# Revit family: Trim_Kit-American_Standard-Delancey-TU05250X_Series
name_source: partatom
category: Plumbing Fixtures
revit_build: Autodesk Revit 2014 (Build: 20130308_1515(x64)
units: mm (PartAtom-declared; Revit-internal decimal feet)

## types (20) — shared parameters
Assembly Code = D2020300
CW Connection = Yes
CWFU = 3
Cold Water Connection Diameter = 1/2"
Cold Water Connection Radius = 1/4"
Default Elevation = 44"
HW Connection = Yes
HWFU = 3
Height = 74"
Hot Water Connection Diameter = 1"
Hot Water Connection Radius = 1/4"
Installation Type = Wall Mounted
Length = 9 1/2"
Manufacturer = American Standard
Price = Prices may vary. Please consult Manufacturer Representative for most up-to-date price list.
URL = https://www.americanstandard-us.com
Valve Trim = Yes
Vent Connection = No
WFU = 4
Warranty Information = Limited Lifetime Function and Finish Warranty
Waste Connection = No
Water Connection Diameter = 1/2"
Water Connection Radius = 1/4"
Width = 7 13/16"

## per-type parameters (varying)
| type | ADA Compliant | Description | Diverter | Finish | Flow Rate | Material | Showerhead | Tub Spout |
| TU052500.002 | Yes | Delancey Trim Kit | No | Metal-American Standard-002-Polished Chrome | 2.5 gpm (9.5 L/min) | Metal-American Standard-002-Polished Chrome | No | No |
| TU052500.295 | Yes | Delancey Trim Kit | No | Metal-American Standard-295-Brushed Nickel | 2.5 gpm (9.5 L/min) | Metal-American Standard-295-Brushed Nickel | No | No |
| TU052500.013 | Yes | Delancey Trim Kit | No | Metal-American Standard-013-Polished Nickel | 2.5 gpm (9.5 L/min) | Metal-American Standard-013-Polished Nickel | No | No |
| TU052500.278 | Yes | Delancey Trim Kit | No | Metal-American Standard-278-Legacy Bronze | 2.5 gpm (9.5 L/min) | Metal-American Standard-278-Legacy Bronze | No | No |
| TU052501.002 | Yes | Delancey Shower Trim | No | Metal-American Standard-002-Polished Chrome | 2.5 gpm (9.5 L/min) | Metal-American Standard-002-Polished Chrome | Yes | No |
| TU052501.013 | Yes | Delancey Shower Trim | No | Metal-American Standard-013-Polished Nickel | 2.5 gpm (9.5 L/min) | Metal-American Standard-013-Polished Nickel | Yes | No |
| TU052501.278 | Yes | Delancey Shower Trim | No | Metal-American Standard-278-Legacy Bronze | 2.5 gpm (9.5 L/min) | Metal-American Standard-278-Legacy Bronze | Yes | No |
| TU052501.295 | Yes | Delancey Shower Trim | No | Metal-American Standard-295-Brushed Nickel | 2.5 gpm (9.5 L/min) | Metal-American Standard-295-Brushed Nickel | Yes | No |
| TU052502.002 | No | Delancey Bath/Shower Trim | Yes | Metal-American Standard-002-Polished Chrome | 2.5 gpm (9.5 L/min) | Metal-American Standard-002-Polished Chrome | Yes | Yes |
| TU052502.013 | No | Delancey Bath/Shower Trim | Yes | Metal-American Standard-013-Polished Nickel | 2.5 gpm (9.5 L/min) | Metal-American Standard-013-Polished Nickel | Yes | Yes |
| TU052502.278 | No | Delancey Bath/Shower Trim | Yes | Metal-American Standard-278-Legacy Bronze | 2.5 gpm (9.5 L/min) | Metal-American Standard-278-Legacy Bronze | Yes | Yes |
| TU052502.295 | No | Delancey Bath/Shower Trim | Yes | Metal-American Standard-295-Brushed Nickel | 2.5 gpm (9.5 L/min) | Metal-American Standard-295-Brushed Nickel | Yes | Yes |
| TU052507.002 | Yes | Delancey Water-Saving Shower Trim | No | Metal-American Standard-002-Polished Chrome | 1.8 gpm (6.8 L/min) | Metal-American Standard-002-Polished Chrome | Yes | No |
| TU052507.013 | Yes | Delancey Water-Saving Shower Trim | No | Metal-American Standard-013-Polished Nickel | 1.8 gpm (6.8 L/min) | Metal-American Standard-013-Polished Nickel | Yes | No |
| TU052507.278 | Yes | Delancey Water-Saving Shower Trim | No | Metal-American Standard-278-Legacy Bronze | 1.8 gpm (6.8 L/min) | Metal-American Standard-278-Legacy Bronze | Yes | No |
| TU052507.295 | Yes | Delancey Water-Saving Shower Trim | No | Metal-American Standard-295-Brushed Nickel | 1.8 gpm (6.8 L/min) | Metal-American Standard-295-Brushed Nickel | Yes | No |
| TU052508.002 | Yes | Delancey Water-Saving Bath/Shower Trim | Yes | Metal-American Standard-002-Polished Chrome | 1.8 gpm (6.8 L/min) | Metal-American Standard-002-Polished Chrome | Yes | Yes |
| TU052508.013 | Yes | Delancey Water-Saving Bath/Shower Trim | Yes | Metal-American Standard-013-Polished Nickel | 1.8 gpm (6.8 L/min) | Metal-American Standard-013-Polished Nickel | Yes | Yes |
| TU052508.278 | Yes | Delancey Water-Saving Bath/Shower Trim | Yes | Metal-American Standard-278-Legacy Bronze | 1.8 gpm (6.8 L/min) | Metal-American Standard-278-Legacy Bronze | Yes | Yes |
| TU052508.295 | Yes | Delancey Water-Saving Bath/Shower Trim | Yes | Metal-American Standard-295-Brushed Nickel | 1.8 gpm (6.8 L/min) | Metal-American Standard-295-Brushed Nickel | Yes | Yes |

note: column(s) folded — value = type name in every type: Model

## geometry (parser evidence)
native form markers: Sweep x1
no freeform markers — native parametric forms only
